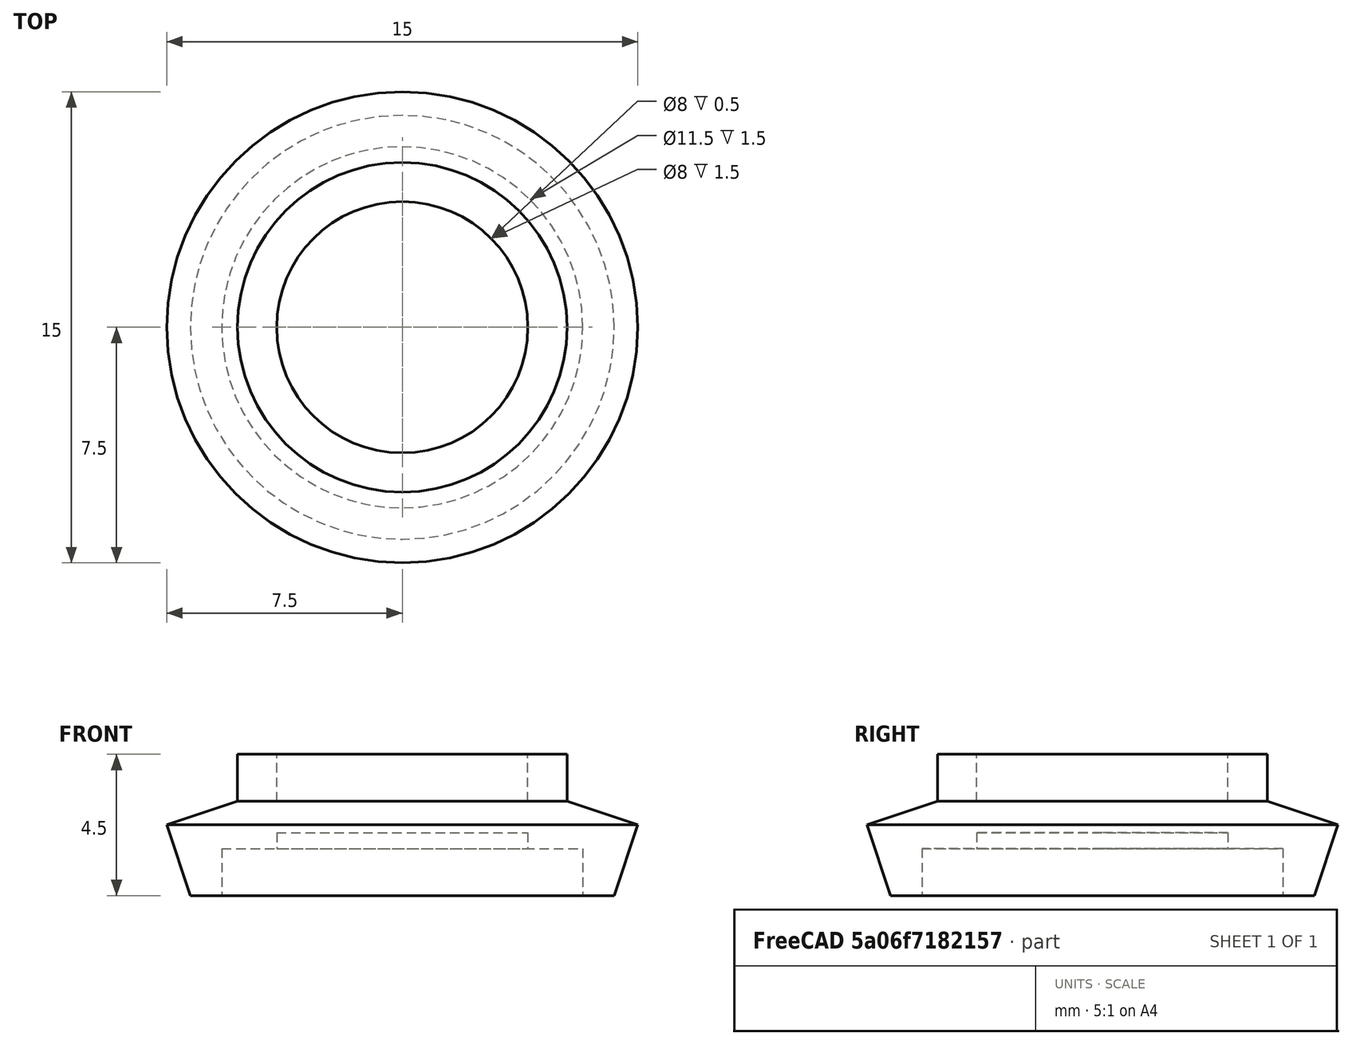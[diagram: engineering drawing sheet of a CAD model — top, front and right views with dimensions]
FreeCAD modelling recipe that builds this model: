
FCSTD DOCUMENT  (FreeCAD 0.21R33771 (Git))
Label: resource-carrier
License: All rights reserved
LicenseURL: http://en.wikipedia.org/wiki/All_rights_reserved
objects: Sketcher::SketchObject×1, PartDesign::Revolution×1, PartDesign::Body×1
note: 4 computed .brp shape members not serialized (recipe doc carries the construction recipe); baked Part::Feature solids carry a one-line shape summary decoded from their .brp

FEATURE [Sketcher::SketchObject] Sketch
  FullyConstrained = true
  MapMode = 5
  Placement = pos=(0,0,0) rot=(1,0,0;1.5708rad)
  Support = -> [XZ_Plane]
  sketch-geometry (12):
    g0: LineSegment StartX=-7.5 StartY=-0.25 StartZ=0 EndX=-5.25 EndY=0.5 EndZ=0
    g1: LineSegment StartX=-7.5 StartY=-0.25 StartZ=0 EndX=-6.75 EndY=-2.5 EndZ=0
    g2: LineSegment StartX=0 StartY=0.5 StartZ=0 EndX=-4 EndY=0.5 EndZ=0
    g3: LineSegment StartX=-4 StartY=0.5 StartZ=0 EndX=-4 EndY=2 EndZ=0
    g4: LineSegment StartX=-4 StartY=2 StartZ=0 EndX=-5.25 EndY=2 EndZ=0
    g5: LineSegment StartX=-5.25 StartY=2 StartZ=0 EndX=-5.25 EndY=0.5 EndZ=0
    g6: LineSegment StartX=0 StartY=-0.5 StartZ=0 EndX=-4 EndY=-0.5 EndZ=0
    g7: LineSegment StartX=-4 StartY=-0.5 StartZ=0 EndX=-4 EndY=-1 EndZ=0
    g8: LineSegment StartX=-4 StartY=-1 StartZ=0 EndX=-5.75 EndY=-1 EndZ=0
    g9: LineSegment StartX=-5.75 StartY=-1 StartZ=0 EndX=-5.75 EndY=-2.5 EndZ=0
    g10: LineSegment StartX=0 StartY=0.5 StartZ=0 EndX=0 EndY=-0.5 EndZ=0
    g11: LineSegment StartX=-5.75 StartY=-2.5 StartZ=0 EndX=-6.75 EndY=-2.5 EndZ=0
  constraints (35):
    c: Coincident(g1,g0)
    c: DistanceX(g0,g-1) = 7.5
    c: PointOnObject(g2,g-2)
    c: Horizontal(g2)
    c: DistanceX(g2,g2) = 4
    c: Coincident(g3,g2)
    c: Vertical(g3)
    c: DistanceY(g3,g3) = 1.5
    c: Coincident(g4,g3)
    c: Horizontal(g4)
    c: DistanceX(g4,g4) = 1.25
    c: Coincident(g5,g4)
    c: Vertical(g5)
    c: Coincident(g0,g5)
    c: Horizontal(g6)
    c: DistanceX(g6,g6) = 4
    c: DistanceY(g5,g5) = 1.5
    c: Coincident(g7,g6)
    c: Vertical(g7)
    c: DistanceY(g7,g7) = 0.5
    c: Coincident(g8,g7)
    c: Horizontal(g8)
    c: DistanceX(g8,g8) = 1.75
    c: Coincident(g9,g8)
    c: Vertical(g9)
    c: DistanceY(g9,g9) = 1.5
    c: Coincident(g10,g2)
    c: Coincident(g10,g6)
    c: DistanceY(g10,g10) = 1
    c: Symmetric(g2,g6,g-1)
    c: Coincident(g11,g9)
    c: Horizontal(g11)
    c: Coincident(g11,g1)
    c: DistanceX(g11,g11) = 1
    c: DistanceY(g0,g-1) = 0.25
FEATURE [PartDesign::Revolution] Revolution
  Angle = 360
  Axis = (0,-2e-16,1)
  Base = (0,0,0)
  Placement = pos=(0,0,0) rot=(1,0,0;1.5708rad)
  Profile = -> Sketch
  ReferenceAxis = -> Sketch [V_Axis]
FEATURE [PartDesign::Body] Body
  Group = -> [Sketch,Revolution]
  Origin = -> Origin
  Tip = -> Revolution
